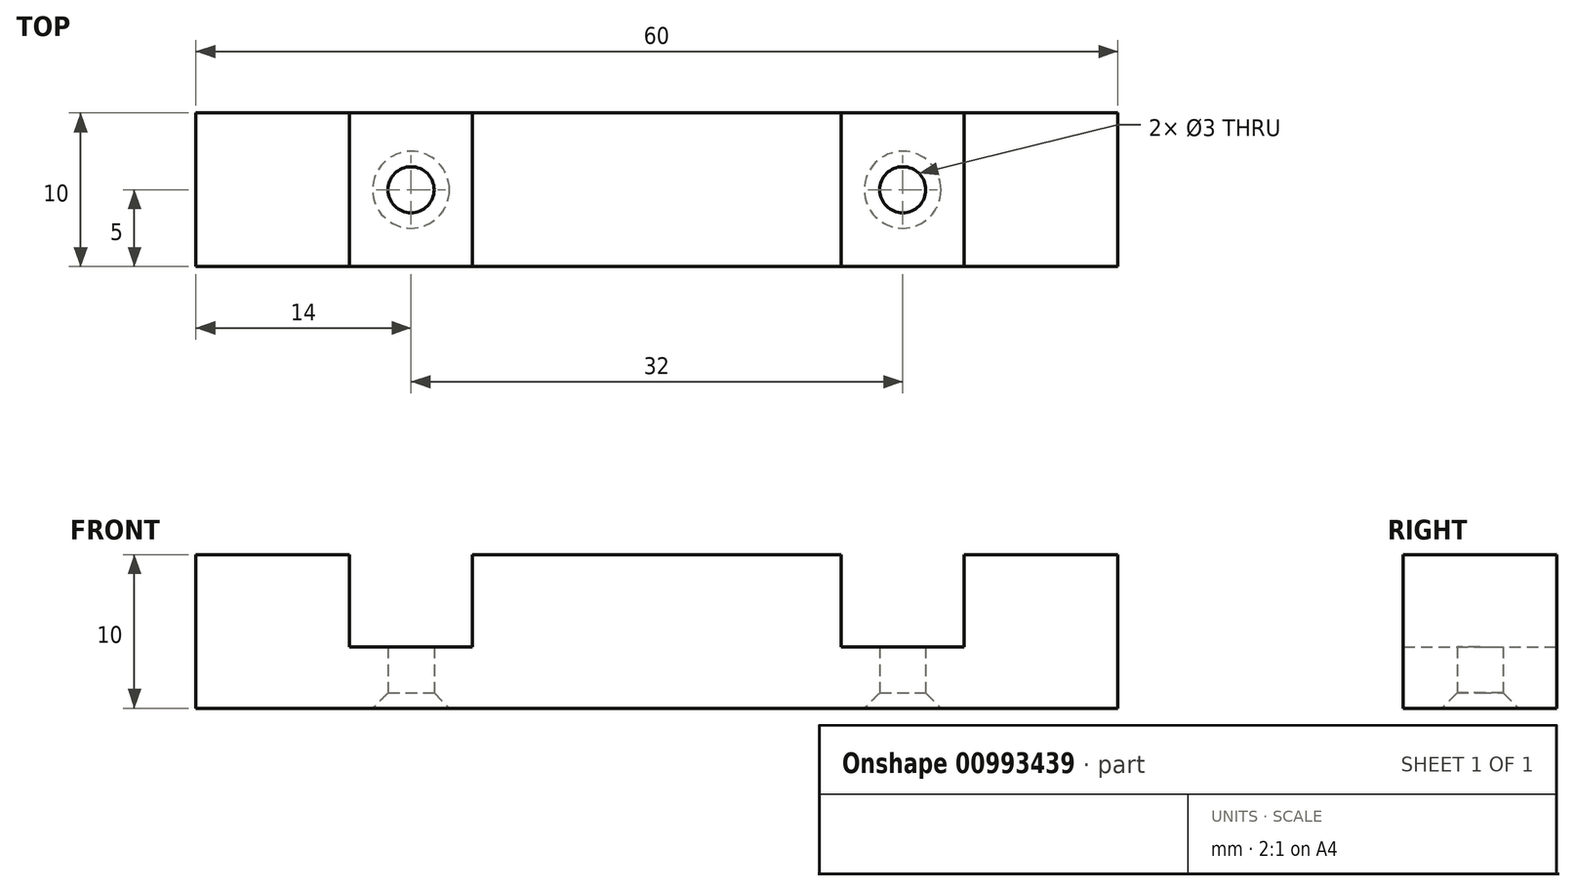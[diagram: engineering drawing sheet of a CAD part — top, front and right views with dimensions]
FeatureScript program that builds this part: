
annotation { "Feature Type Name" : "Feature", "Feature Type Description" : "" }
export const myFeature = defineFeature(function(context is Context, id is Id, definition is map)
    precondition{}
    {
        {
            var Q0;
            Q0=qCreatedBy(makeId("Top.planeOp"),FACE);
            var sketch = newSketch(context, id + "F0", { "sketchPlane" : qUnion([Q0])});
            skLineSegment(sketch, "E0.bottom", {"start": v(-30, -5) * mm, "end": v(30, -5) * mm});
            skLineSegment(sketch, "E0.top", {"start": v(-30, 5) * mm, "end": v(30, 5) * mm});
            skLineSegment(sketch, "E0.left", {"start": v(-30, -5) * mm, "end": v(-30, 5) * mm});
            skLineSegment(sketch, "E0.right", {"start": v(30, -5) * mm, "end": v(30, 5) * mm});
            skPoint(sketch, "E0.middle", {"position": v(0, 0) * mm});
            skSolve(sketch);
        }
        {
            var Q0;
            Q0=makeQuery(id+"F0.imprint","IMPRINT",FACE,{"disambiguationData":[TD([[makeQuery(id+"F0.imprint","IMPRINT",EDGE,{"derivedFrom":sQuery(id+"F0.wireOp",EDGE,"E0.bottom")}),1.0]])]});
            extrude(context, id + "F1", {"entities" : qUnion([Q0]), "depth" : 4 * mm, "offsetDistance" : 25 * mm});
        }
        {
            var Q0;
            Q0=makeQuery(id+"F1.opExtrude","CAP_FACE",FACE,{"disambiguationData":[OSD([sQuery(id+"F0.wireOp",EDGE,"E0.bottom"),sQuery(id+"F0.wireOp",EDGE,"E0.top"),sQuery(id+"F0.wireOp",EDGE,"E0.left"),sQuery(id+"F0.wireOp",EDGE,"E0.right")])],"isStart":false});
            var sketch = newSketch(context, id + "F2", { "sketchPlane" : qUnion([Q0])});
            skLineSegment(sketch, "E1.bottom", {"start": v(-30, -5) * mm, "end": v(-20, -5) * mm});
            skLineSegment(sketch, "E1.top", {"start": v(-30, 5) * mm, "end": v(-20, 5) * mm});
            skLineSegment(sketch, "E1.left", {"start": v(-30, -5) * mm, "end": v(-30, 5) * mm});
            skLineSegment(sketch, "E1.right", {"start": v(-20, -5) * mm, "end": v(-20, 5) * mm});
            skPoint(sketch, "E1.middle", {"position": v(-25, 0) * mm});
            skLineSegment(sketch, "E2.bottom", {"start": v(-12, -5) * mm, "end": v(12, -5) * mm});
            skLineSegment(sketch, "E2.top", {"start": v(-12, 5) * mm, "end": v(12, 5) * mm});
            skLineSegment(sketch, "E2.left", {"start": v(-12, -5) * mm, "end": v(-12, 5) * mm});
            skLineSegment(sketch, "E2.right", {"start": v(12, -5) * mm, "end": v(12, 5) * mm});
            skPoint(sketch, "E2.middle", {"position": v(0, 0) * mm});
            skLineSegment(sketch, "E3.bottom", {"start": v(20, -5) * mm, "end": v(30, -5) * mm});
            skLineSegment(sketch, "E3.top", {"start": v(20, 5) * mm, "end": v(30, 5) * mm});
            skLineSegment(sketch, "E3.left", {"start": v(20, -5) * mm, "end": v(20, 5) * mm});
            skLineSegment(sketch, "E3.right", {"start": v(30, -5) * mm, "end": v(30, 5) * mm});
            skPoint(sketch, "E3.middle", {"position": v(25, 0) * mm});
            skSolve(sketch);
        }
        {
            var Q0;
            Q0=makeQuery(id+"F2.imprint","IMPRINT",FACE,{"disambiguationData":[TD([[makeQuery(id+"F2.imprint","IMPRINT",EDGE,{"derivedFrom":sQuery(id+"F2.wireOp",EDGE,"E1.bottom")}),1.0]])]});
            var Q1;
            Q1=makeQuery(id+"F2.imprint","IMPRINT",FACE,{"disambiguationData":[TD([[makeQuery(id+"F2.imprint","IMPRINT",EDGE,{"derivedFrom":sQuery(id+"F2.wireOp",EDGE,"E2.bottom")}),1.0]])]});
            var Q2;
            Q2=makeQuery(id+"F2.imprint","IMPRINT",FACE,{"disambiguationData":[TD([[makeQuery(id+"F2.imprint","IMPRINT",EDGE,{"derivedFrom":sQuery(id+"F2.wireOp",EDGE,"E3.bottom")}),1.0]])]});
            extrude(context, id + "F3", {"entities" : qUnion([Q0, Q1, Q2]), "operationType" : NewBodyOperationType.ADD, "depth" : 6 * mm, "offsetDistance" : 25 * mm});
        }
        {
            var Q0;
            Q0=makeQuery(id+"F1.opExtrude","CAP_FACE",FACE,{"disambiguationData":[OSD([sQuery(id+"F0.wireOp",EDGE,"E0.bottom"),sQuery(id+"F0.wireOp",EDGE,"E0.top"),sQuery(id+"F0.wireOp",EDGE,"E0.left"),sQuery(id+"F0.wireOp",EDGE,"E0.right")])],"isStart":true});
            var sketch = newSketch(context, id + "F4", { "sketchPlane" : qUnion([Q0])});
            skCircle(sketch, "E4", {"center": v(-16, 0) * mm, "radius": 1.5 * mm});
            skCircle(sketch, "E5", {"center": v(16, 0) * mm, "radius": 1.5 * mm});
            skSolve(sketch);
        }
        {
            var Q0;
            Q0=sQuery(id+"F4.wireOp",VERTEX,"E4.center");
            var Q1;
            Q1=sQuery(id+"F4.wireOp",VERTEX,"E5.center");
            var Q2;
            Q2=makeQuery(id+"F1.opExtrude","SWEPT_BODY",BODY,{"disambiguationData":[OSD([sQuery(id+"F0.wireOp",EDGE,"E0.bottom"),sQuery(id+"F0.wireOp",EDGE,"E0.top"),sQuery(id+"F0.wireOp",EDGE,"E0.left"),sQuery(id+"F0.wireOp",EDGE,"E0.right")])]});
            hole(context, id + "F5", {"style" : HoleStyle.C_SINK, "endStyle" : HoleEndStyle.THROUGH, "holeDiameter" : 3 * mm, "cSinkDiameter" : 5 * mm, "cSinkAngle" : 90 * degree, "majorDiameter" : 5 * mm, "isTappedThrough" : true, "tappedDepth" : 12 * mm, "tapClearance" : 3, "locations" : qUnion([Q0, Q1]), "scope" : qUnion([Q2])});
        }
    });
